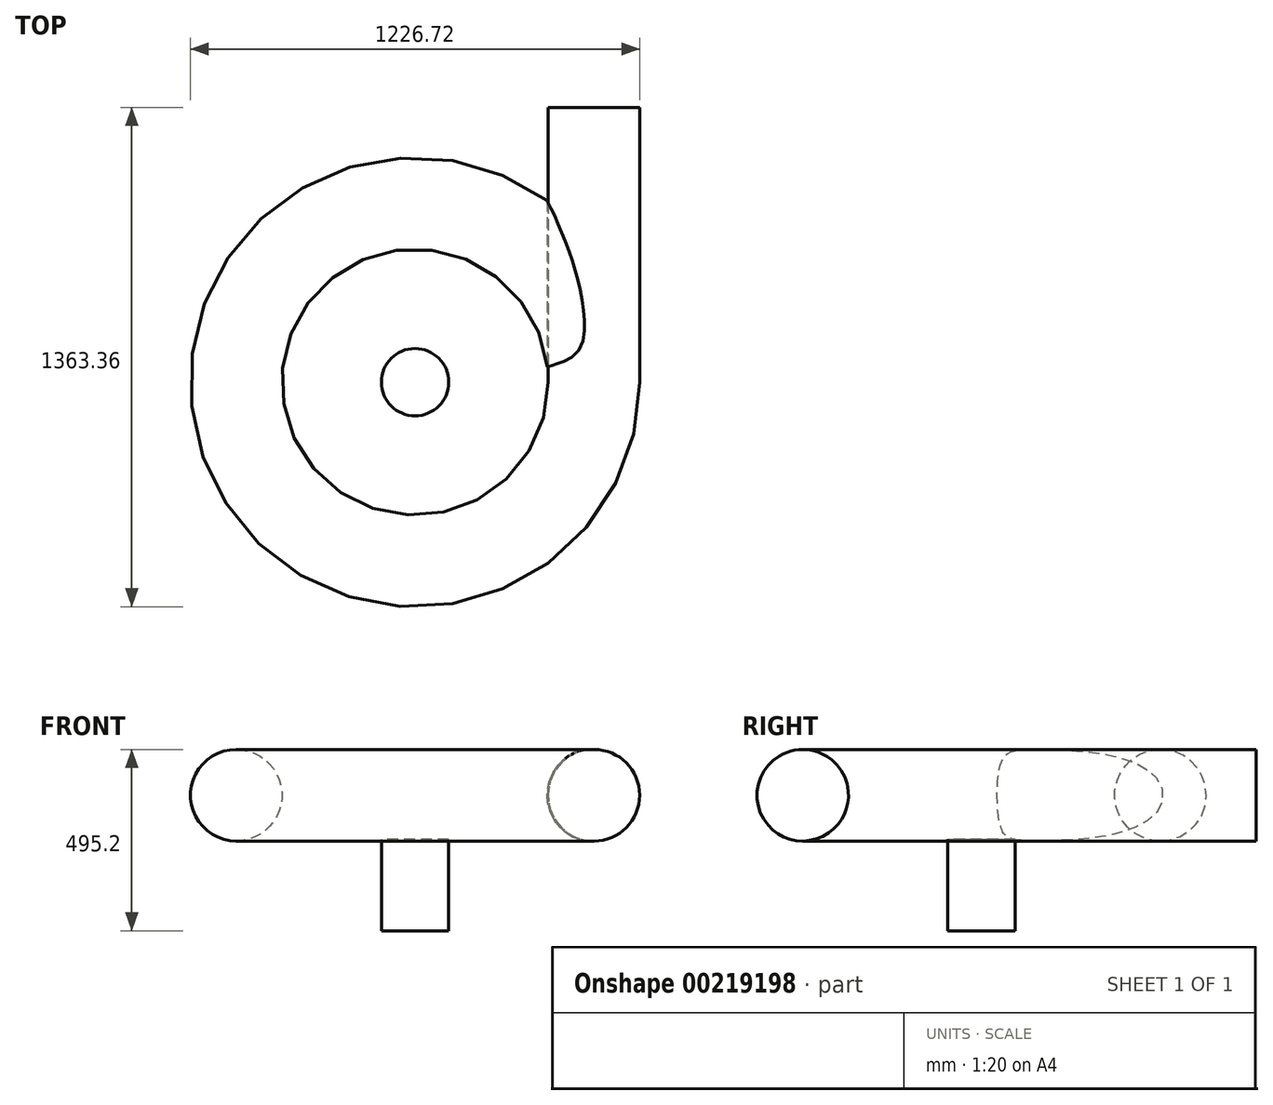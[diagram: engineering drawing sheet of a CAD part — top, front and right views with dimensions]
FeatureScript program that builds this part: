
annotation { "Feature Type Name" : "Feature", "Feature Type Description" : "" }
export const myFeature = defineFeature(function(context is Context, id is Id, definition is map)
    precondition{}
    {
        {
            var Q0;
            Q0=qCreatedBy(makeId("Front.planeOp"),FACE);
            var sketch = newSketch(context, id + "F0", { "sketchPlane" : qUnion([Q0])});
            skLineSegment(sketch, "E0", {"start": v(365, 40.4) * mm, "end": v(365, 0) * mm});
            skLineSegment(sketch, "E1.bottom", {"start": v(0, -100) * mm, "end": v(-92, -100) * mm});
            skLineSegment(sketch, "E1.top", {"start": v(0, -350) * mm, "end": v(-92, -350) * mm});
            skLineSegment(sketch, "E1.left", {"start": v(0, -100) * mm, "end": v(0, -350) * mm});
            skLineSegment(sketch, "E1.right", {"start": v(-92, -100) * mm, "end": v(-92, -350) * mm});
            skCircle(sketch, "E2", {"center": v(488.36, 20.2) * mm, "radius": 125 * mm});
            skPoint(sketch, "E2.third.point", {"position": v(366.7, -8.5) * mm});
            skCircle(sketch, "E3", {"center": v(488.36, 20.2) * mm, "radius": 127.5 * mm});
            skSolve(sketch);
        }
        {
            var Q0;
            {var subQ0=sQuery(id+"F0.wireOp",EDGE,"E0");Q0=makeQuery(id+"F0.imprint","IMPRINT",FACE,{"disambiguationData":[TD([[makeQuery(id+"F0.imprint","IMPRINT",EDGE,{"derivedFrom":subQ0}),-1.0]])]});}
            var Q1;
            Q1=makeQuery(id+"F0.imprint","IMPRINT",FACE,{"disambiguationData":[TD([[makeQuery(id+"F0.imprint","IMPRINT",EDGE,{"derivedFrom":sQuery(id+"F0.wireOp",EDGE,"E1.bottom")}),1.0]])]});
            var Q2;
            {var subQ0=sQuery(id+"F0.wireOp",EDGE,"E0");Q2=makeQuery(id+"F0.imprint","IMPRINT",FACE,{"disambiguationData":[TD([[makeQuery(id+"F0.imprint","IMPRINT",EDGE,{"derivedFrom":subQ0}),1.0]])]});}
            var Q3;
            Q3=sQuery(id+"F0.wireOp",EDGE,"E1.left");
            revolve(context, id + "F1", {"entities" : qUnion([Q0, Q1, Q2]), "axis" : qUnion([Q3]), "revolveType" : RevolveType.FULL});
        }
        {
            var Q0;
            {var subQ0=sQuery(id+"F0.wireOp",EDGE,"E0");Q0=makeQuery(id+"F0.imprint","IMPRINT",FACE,{"disambiguationData":[TD([[makeQuery(id+"F0.imprint","IMPRINT",EDGE,{"derivedFrom":subQ0}),-1.0]])]});}
            var Q1;
            {var subQ0=sQuery(id+"F0.wireOp",EDGE,"E0");Q1=makeQuery(id+"F0.imprint","IMPRINT",FACE,{"disambiguationData":[TD([[makeQuery(id+"F0.imprint","IMPRINT",EDGE,{"derivedFrom":subQ0}),1.0]])]});}
            extrude(context, id + "F2", {"entities" : qUnion([Q0, Q1]), "operationType" : NewBodyOperationType.ADD, "oppositeDirection" : true, "depth" : 750 * mm});
        }
        {
            var Q0;
            Q0=makeQuery(id+"F0.imprint","IMPRINT",FACE,{"disambiguationData":[TD([[makeQuery(id+"F0.imprint","IMPRINT",EDGE,{"derivedFrom":sQuery(id+"F0.wireOp",EDGE,"E3")}),1.0]])]});
            extrude(context, id + "F3", {"entities" : qUnion([Q0]), "operationType" : NewBodyOperationType.REMOVE, "oppositeDirection" : true, "depth" : 750 * mm});
        }
    });
